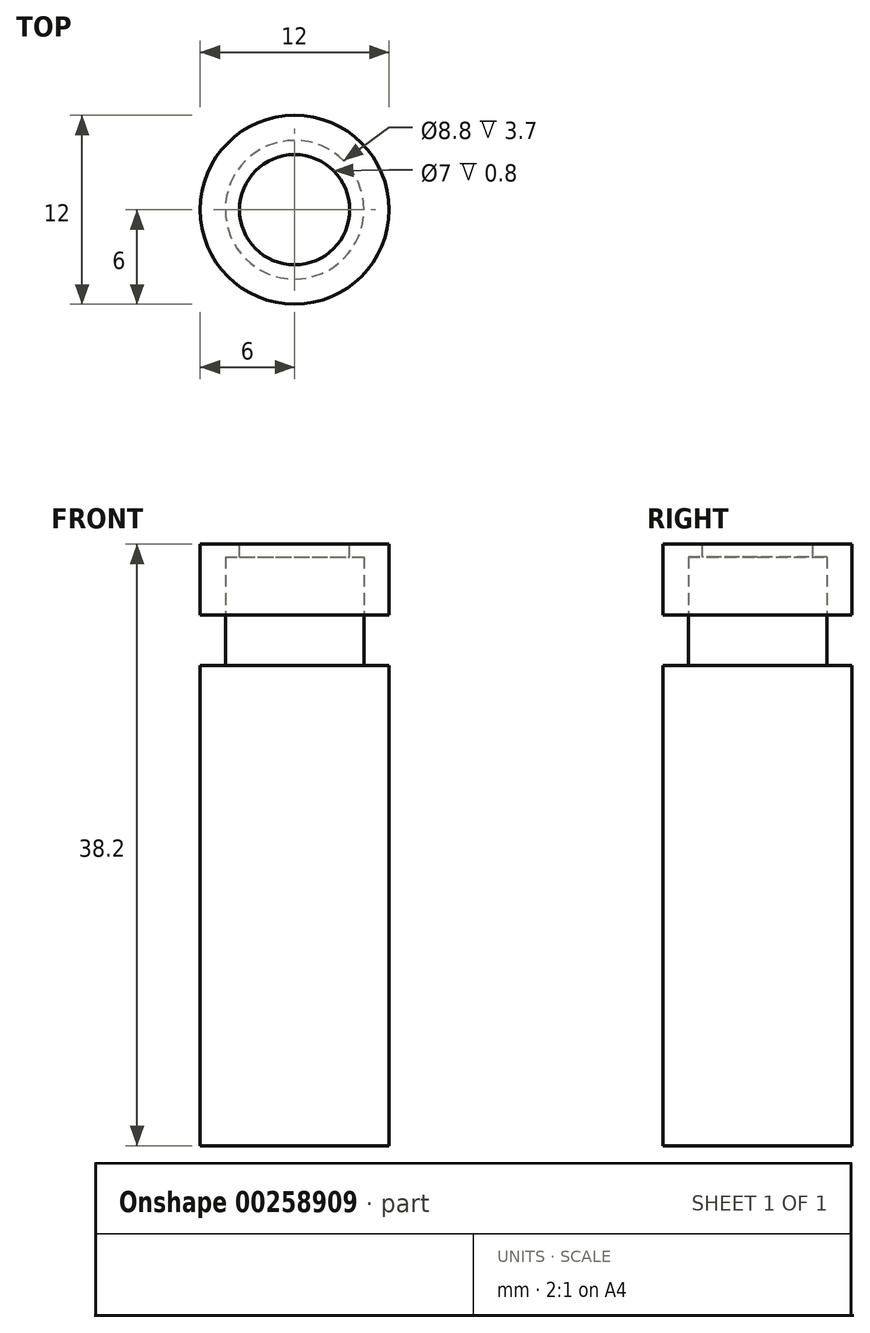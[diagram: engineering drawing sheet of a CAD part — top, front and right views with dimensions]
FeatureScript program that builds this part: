
annotation { "Feature Type Name" : "Feature", "Feature Type Description" : "" }
export const myFeature = defineFeature(function(context is Context, id is Id, definition is map)
    precondition{}
    {
        {
            var Q0;
            Q0=qCreatedBy(makeId("Top.planeOp"),FACE);
            var sketch = newSketch(context, id + "F0", { "sketchPlane" : qUnion([Q0])});
            skCircle(sketch, "E0", {"center": v(0, 0) * mm, "radius": 6 * mm});
            skSolve(sketch);
        }
        {
            var Q0;
            Q0 = qSketchRegion(id + "F0", true);
            extrude(context, id + "F1", {"entities" : qUnion([Q0]), "depth" : 30.5 * mm});
        }
        {
            var Q0;
            Q0=makeQuery(id+"F1.opExtrude","CAP_FACE",FACE,{"disambiguationData":[OSD([sQuery(id+"F0.wireOp",EDGE,"E0")])],"isStart":false});
            var sketch = newSketch(context, id + "F2", { "sketchPlane" : qUnion([Q0])});
            skCircle(sketch, "E1", {"center": v(0, 0) * mm, "radius": 4.4 * mm});
            skSolve(sketch);
        }
        {
            var Q0;
            Q0 = qSketchRegion(id + "F2", true);
            extrude(context, id + "F3", {"entities" : qUnion([Q0]), "operationType" : NewBodyOperationType.ADD, "depth" : 3.2 * mm});
        }
        {
            var Q0;
            Q0=makeQuery(id+"F3.opExtrude","CAP_FACE",FACE,{"disambiguationData":[OSD([sQuery(id+"F2.wireOp",EDGE,"E1")])],"isStart":false});
            var sketch = newSketch(context, id + "F4", { "sketchPlane" : qUnion([Q0])});
            skCircle(sketch, "E2", {"center": v(0, 0) * mm, "radius": 6 * mm});
            skSolve(sketch);
        }
        {
            var Q0;
            Q0 = qSketchRegion(id + "F4", true);
            extrude(context, id + "F5", {"entities" : qUnion([Q0]), "depth" : 4.5 * mm});
        }
        {
            var Q0;
            Q0=makeQuery(id+"F5.opExtrude","CAP_FACE",FACE,{"disambiguationData":[OSD([sQuery(id+"F4.wireOp",EDGE,"E2")])],"isStart":true});
            var sketch = newSketch(context, id + "F6", { "sketchPlane" : qUnion([Q0])});
            skCircle(sketch, "E3.0", {"center": v(0, 0) * mm, "radius": 4.4 * mm});
            skSolve(sketch);
        }
        {
            var Q0;
            Q0 = qSketchRegion(id + "F6", true);
            extrude(context, id + "F7", {"entities" : qUnion([Q0]), "operationType" : NewBodyOperationType.REMOVE, "oppositeDirection" : true, "depth" : 3.7 * mm});
        }
        {
            var Q0;
            Q0=makeQuery(id+"F5.opExtrude","CAP_FACE",FACE,{"disambiguationData":[OSD([sQuery(id+"F4.wireOp",EDGE,"E2")])],"isStart":false});
            var sketch = newSketch(context, id + "F8", { "sketchPlane" : qUnion([Q0])});
            skCircle(sketch, "E4", {"center": v(0, 0) * mm, "radius": 3.5 * mm});
            skSolve(sketch);
        }
        {
            var Q0;
            Q0 = qSketchRegion(id + "F8", true);
            extrude(context, id + "F9", {"entities" : qUnion([Q0]), "operationType" : NewBodyOperationType.REMOVE, "oppositeDirection" : true, "depth" : 1 * mm});
        }
    });
